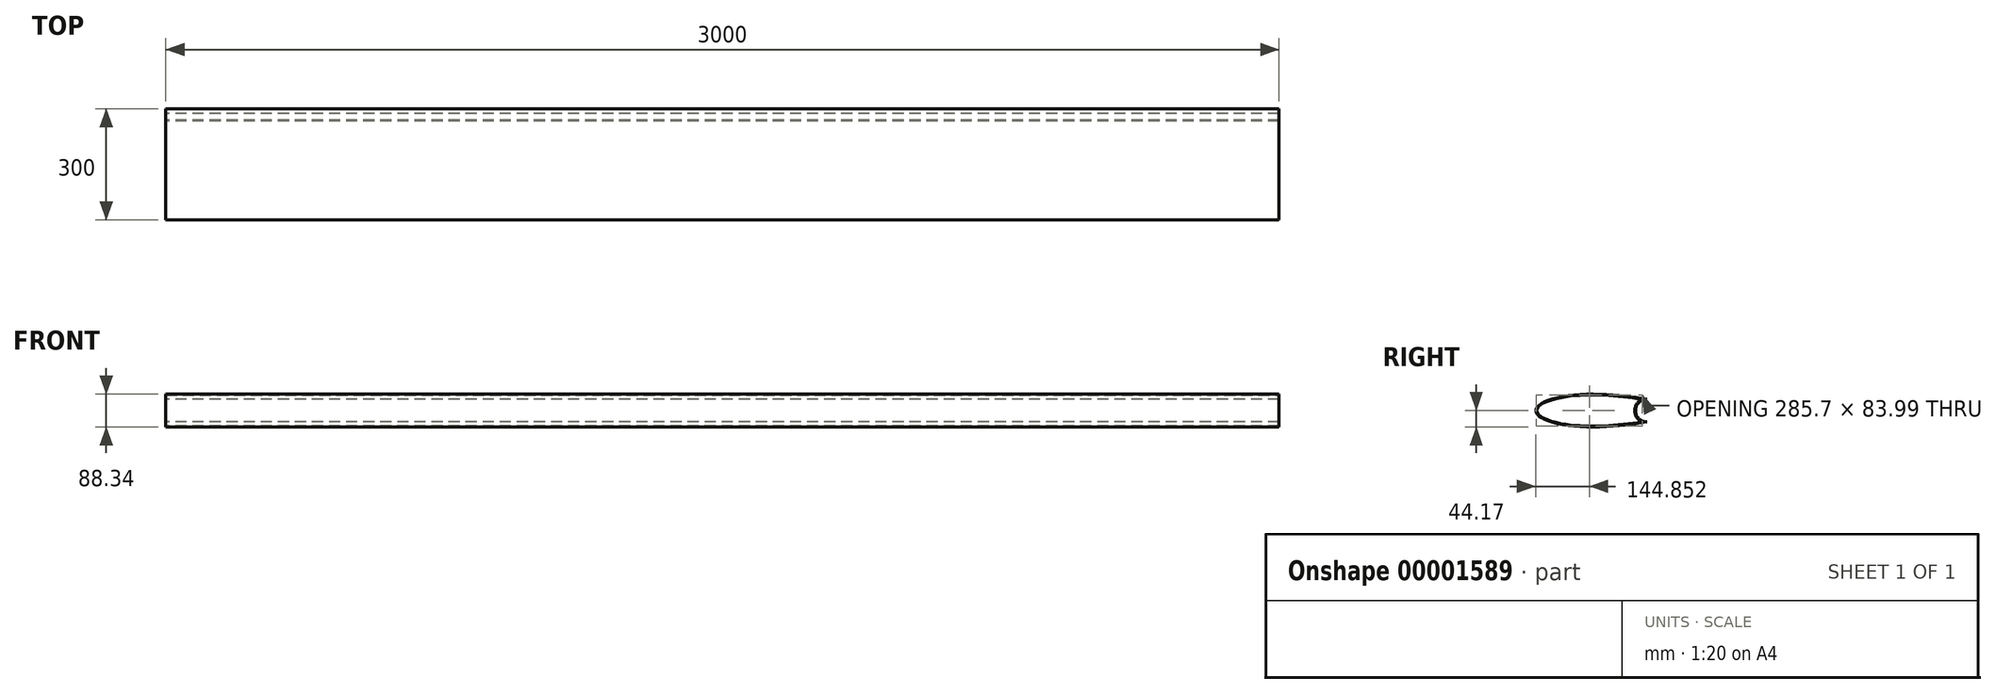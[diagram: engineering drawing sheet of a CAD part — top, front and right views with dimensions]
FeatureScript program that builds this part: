
annotation { "Feature Type Name" : "Feature", "Feature Type Description" : "" }
export const myFeature = defineFeature(function(context is Context, id is Id, definition is map)
    precondition{}
    {
        {
            var Q0;
            Q0=qCreatedBy(makeId("Right.planeOp"),FACE);
            var sketch = newSketch(context, id + "F0", { "sketchPlane" : qUnion([Q0])});
            skLineSegment(sketch, "E0", {"start": v(0, 0) * mm, "end": v(300, 0) * mm, "construction": true});
            skFitSpline(sketch, "E1", {"points": [v(300, 31) * mm, v(240.28, 38.85) * mm, v(159.2, 44.14) * mm, v(81.92, 39.26) * mm, v(33.96, 27.73) * mm, v(10.64, 15.94) * mm, v(2.42, 7.36) * mm, v(0, 0) * mm], "startDerivative": vector(-402.73, 52.7) * mm, "endDerivative": vector(0, -146.63) * mm});
            skFitSpline(sketch, "E2.0.MirrorCS", {"points": [v(300, -31) * mm, v(240.28, -38.85) * mm, v(159.2, -44.14) * mm, v(81.92, -39.26) * mm, v(33.96, -27.73) * mm, v(10.64, -15.94) * mm, v(2.42, -7.36) * mm, v(0, 0) * mm], "startDerivative": vector(-402.73, -52.7) * mm, "endDerivative": vector(0, 146.63) * mm});
            skArc(sketch, "E3", {"start": v(300, 31) * mm, "mid": v(269, 0) * mm, "end": v(300, -31) * mm});
            skSolve(sketch);
        }
        {
            var Q0;
            Q0=makeQuery(id+"F0.imprint","IMPRINT",FACE,{"disambiguationData":[TD([[makeQuery(id+"F0.imprint","IMPRINT",EDGE,{"derivedFrom":sQuery(id+"F0.wireOp",EDGE,"E1")}),1.0]])]});
            extrude(context, id + "F1", {"entities" : qUnion([Q0]), "endBound" : BoundingType.SYMMETRIC, "depth" : 3000 * mm});
        }
        {
            var Q0;
            Q0=makeQuery(id+"F1.opExtrude","CAP_FACE",FACE,{"disambiguationData":[OSD([sQuery(id+"F0.wireOp",EDGE,"E1"),sQuery(id+"F0.wireOp",EDGE,"E2.0.MirrorCS"),sQuery(id+"F0.wireOp",EDGE,"E3")])],"isStart":false});
            var Q1;
            Q1=makeQuery(id+"F1.opExtrude","CAP_FACE",FACE,{"disambiguationData":[OSD([sQuery(id+"F0.wireOp",EDGE,"E1"),sQuery(id+"F0.wireOp",EDGE,"E2.0.MirrorCS"),sQuery(id+"F0.wireOp",EDGE,"E3")])],"isStart":true});
            shell(context, id + "F2", {"entities" : qUnion([Q0, Q1]), "thickness" : 2 * mm});
        }
    });
